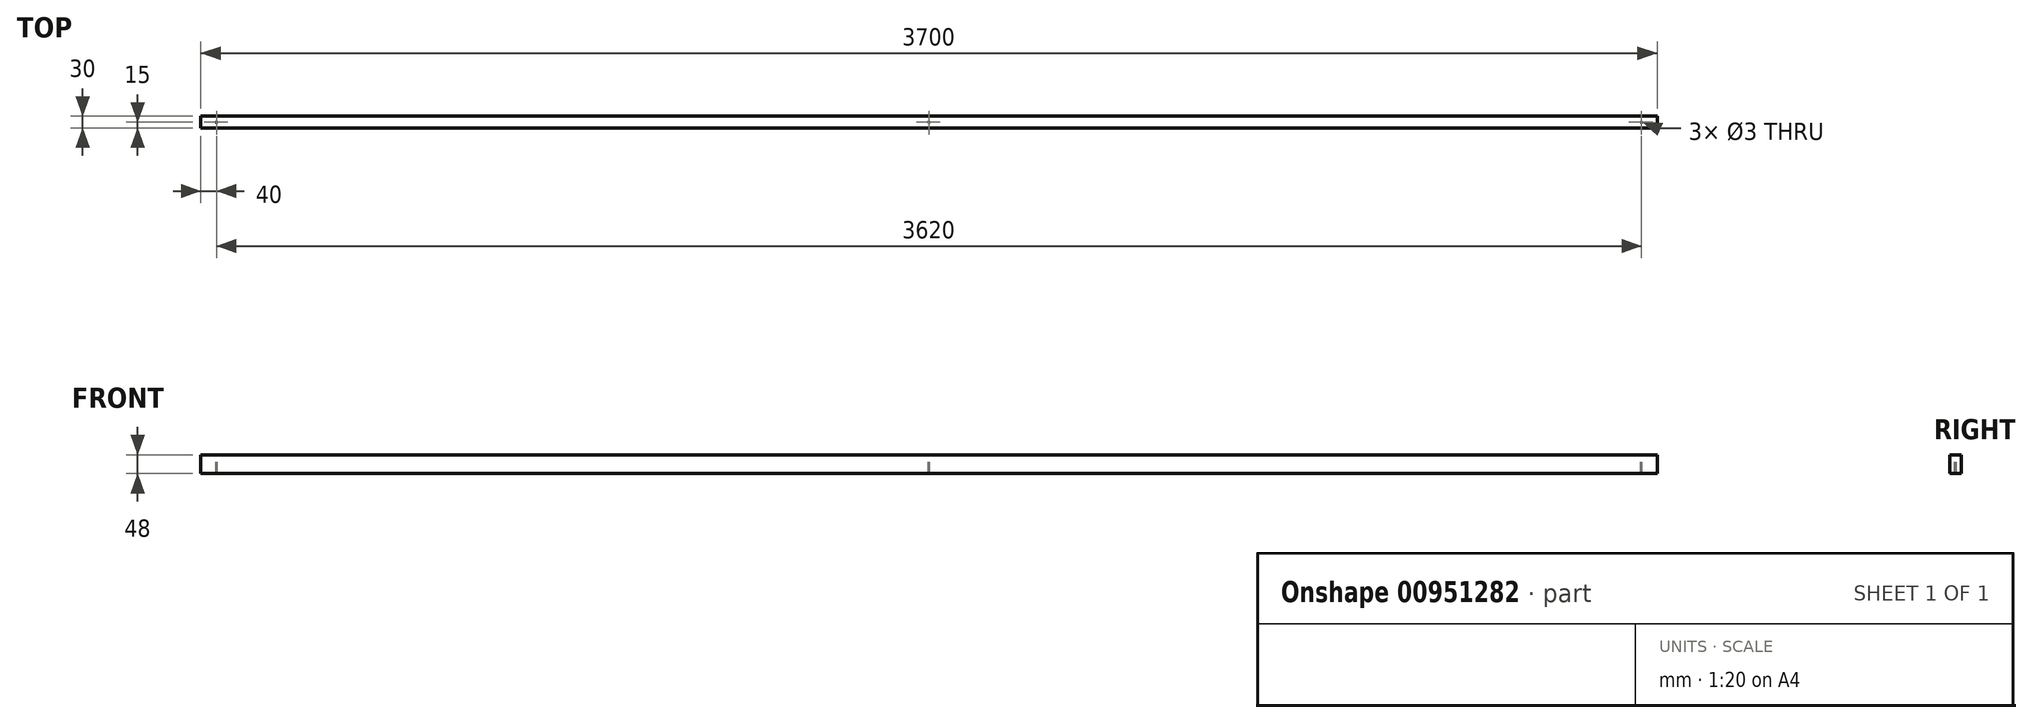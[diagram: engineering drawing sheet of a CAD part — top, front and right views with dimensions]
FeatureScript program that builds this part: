
annotation { "Feature Type Name" : "Feature", "Feature Type Description" : "" }
export const myFeature = defineFeature(function(context is Context, id is Id, definition is map)
    precondition{}
    {
        {
            var Q0;
            Q0=qCreatedBy(makeId("Right.planeOp"),FACE);
            var sketch = newSketch(context, id + "F0", { "sketchPlane" : qUnion([Q0])});
            skLineSegment(sketch, "E0.bottom", {"start": v(15, -24) * mm, "end": v(-15, -24) * mm});
            skLineSegment(sketch, "E0.top", {"start": v(15, 24) * mm, "end": v(-15, 24) * mm});
            skLineSegment(sketch, "E0.left", {"start": v(15, -24) * mm, "end": v(15, 24) * mm});
            skLineSegment(sketch, "E0.right", {"start": v(-15, -24) * mm, "end": v(-15, 24) * mm});
            skPoint(sketch, "E0.middle", {"position": v(0, 0) * mm});
            skSolve(sketch);
        }
        {
            var Q0;
            Q0=makeQuery(id+"F0.imprint","IMPRINT",FACE,{"disambiguationData":[TD([[makeQuery(id+"F0.imprint","IMPRINT",EDGE,{"derivedFrom":sQuery(id+"F0.wireOp",EDGE,"E0.bottom")}),-1.0]])]});
            extrude(context, id + "F1", {"entities" : qUnion([Q0]), "depth" : 3700 * mm, "offsetDistance" : 25 * mm});
        }
        {
            var Q0;
            Q0=makeQuery(id+"F1.opExtrude","SWEPT_FACE",FACE,{"disambiguationData":[OSD([sQuery(id+"F0.wireOp",EDGE,"E0.top")])]});
            var sketch = newSketch(context, id + "F2", { "sketchPlane" : qUnion([Q0])});
            skLineSegment(sketch, "E1", {"start": v(0, 0) * mm, "end": v(40, 0) * mm, "construction": true});
            skLineSegment(sketch, "E2", {"start": v(40, 0) * mm, "end": v(1850, 0) * mm, "construction": true});
            skLineSegment(sketch, "E3", {"start": v(3700, 0) * mm, "end": v(3660, 0) * mm, "construction": true});
            skCircle(sketch, "E4", {"center": v(3660, 0) * mm, "radius": 1.5 * mm});
            skCircle(sketch, "E5", {"center": v(1850, 0) * mm, "radius": 1.5 * mm});
            skCircle(sketch, "E6", {"center": v(40, 0) * mm, "radius": 1.5 * mm});
            skSolve(sketch);
        }
        {
            var Q0;
            Q0=makeQuery(id+"F2.imprint","IMPRINT",FACE,{"disambiguationData":[TD([[makeQuery(id+"F2.imprint","IMPRINT",EDGE,{"derivedFrom":sQuery(id+"F2.wireOp",EDGE,"E6")}),1.0]])]});
            var Q1;
            Q1=makeQuery(id+"F2.imprint","IMPRINT",FACE,{"disambiguationData":[TD([[makeQuery(id+"F2.imprint","IMPRINT",EDGE,{"derivedFrom":sQuery(id+"F2.wireOp",EDGE,"E5")}),1.0]])]});
            var Q2;
            Q2=makeQuery(id+"F2.imprint","IMPRINT",FACE,{"disambiguationData":[TD([[makeQuery(id+"F2.imprint","IMPRINT",EDGE,{"derivedFrom":sQuery(id+"F2.wireOp",EDGE,"E4")}),1.0]])]});
            extrude(context, id + "F3", {"entities" : qUnion([Q0, Q1, Q2]), "operationType" : NewBodyOperationType.REMOVE, "oppositeDirection" : true, "depth" : 50 * mm, "offsetDistance" : 25 * mm});
        }
    });
